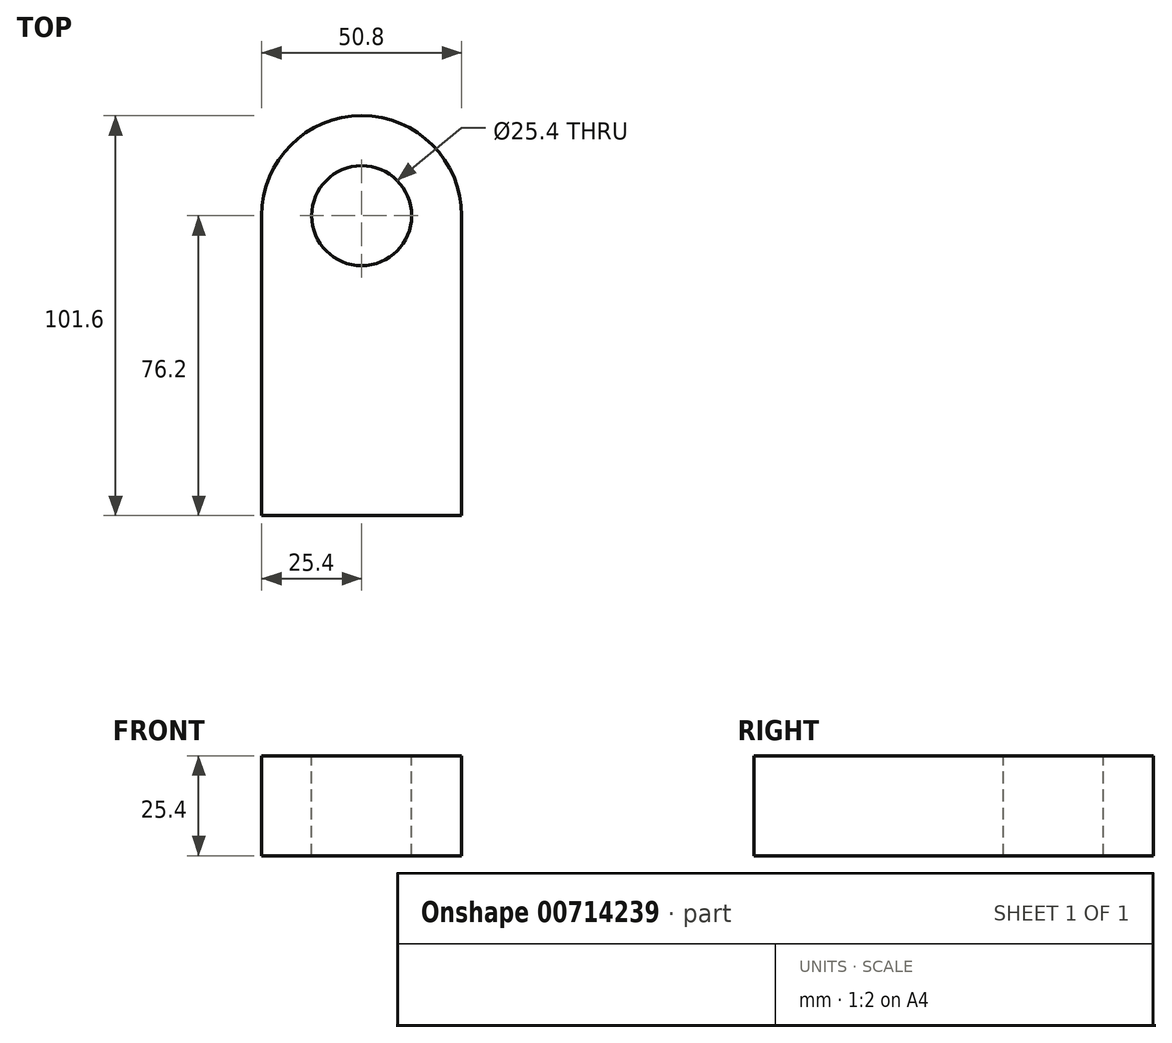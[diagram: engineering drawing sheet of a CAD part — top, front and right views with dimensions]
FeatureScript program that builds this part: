
annotation { "Feature Type Name" : "Feature", "Feature Type Description" : "" }
export const myFeature = defineFeature(function(context is Context, id is Id, definition is map)
    precondition{}
    {
        {
            var Q0;
            Q0=qCreatedBy(makeId("Top.planeOp"),FACE);
            var sketch = newSketch(context, id + "F0", { "sketchPlane" : qUnion([Q0])});
            skLineSegment(sketch, "E0.bottom", {"start": v(-25.4, 0) * mm, "end": v(25.4, 0) * mm});
            skLineSegment(sketch, "E0.top", {"start": v(-25.4, 76.2) * mm, "end": v(25.4, 76.2) * mm});
            skLineSegment(sketch, "E0.left", {"start": v(-25.4, 0) * mm, "end": v(-25.4, 76.2) * mm});
            skLineSegment(sketch, "E0.right", {"start": v(25.4, 0) * mm, "end": v(25.4, 76.2) * mm});
            skCircle(sketch, "E1", {"center": v(0, 76.2) * mm, "radius": 25.4 * mm});
            skSolve(sketch);
        }
        {
            var Q0;
            Q0 = qSketchRegion(id + "F0", true);
            extrude(context, id + "F1", {"entities" : qUnion([Q0]), "depth" : 25.4 * mm, "offsetDistance" : 25.4 * mm});
        }
        {
            var Q0;
            Q0=makeQuery(id+"F1.opExtrude","CAP_FACE",FACE,{"disambiguationData":[OSD([sQuery(id+"F0.wireOp",EDGE,"E0.bottom"),sQuery(id+"F0.wireOp",EDGE,"E0.left"),sQuery(id+"F0.wireOp",EDGE,"E0.right"),sQuery(id+"F0.wireOp",EDGE,"E1")])],"isStart":false});
            var sketch = newSketch(context, id + "F2", { "sketchPlane" : qUnion([Q0])});
            skCircle(sketch, "E2", {"center": v(0, 76.2) * mm, "radius": 12.7 * mm});
            skSolve(sketch);
        }
        {
            var Q0;
            Q0=makeQuery(id+"F2.imprint","IMPRINT",FACE,{"disambiguationData":[TD([[makeQuery(id+"F2.imprint","IMPRINT",EDGE,{"derivedFrom":sQuery(id+"F2.wireOp",EDGE,"E2")}),1.0]])]});
            extrude(context, id + "F3", {"entities" : qUnion([Q0]), "operationType" : NewBodyOperationType.REMOVE, "oppositeDirection" : true, "depth" : 25.4 * mm, "offsetDistance" : 25.4 * mm});
        }
    });
